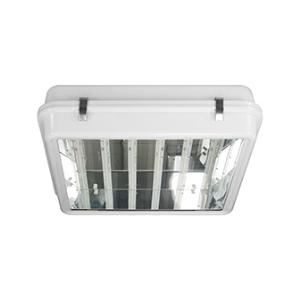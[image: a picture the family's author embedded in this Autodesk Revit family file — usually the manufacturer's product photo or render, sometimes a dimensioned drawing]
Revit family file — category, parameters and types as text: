
# Revit family: 3f_filippi_-_3f_cub_vt_3f_filippi_-_56332_-_3f_cub_led_100w_dali_cr_vt
name_source: partatom
category: Lighting Fixtures
units: mm (PartAtom-declared; Revit-internal decimal feet)

## family parameters
Cut with Voids When Loaded = No
Host = Face
Light Source = No
Part Type = Normal
Room Calculation Point = No
Round Connector Dimension = Use Diameter
Shared = No

## types (1)
- 3F Filippi - 3F Cub VT (1 x LED, 15195 lm, 108 W, 4000 K)
    Apparent Load = 108 VA
    Approval mark = CE
    CIE Flux Codes = 54 85 98 100 100
    Color Rendering = 80
    Color Temperature = 4000 K
    Control Gear = Electronic transformer
    Default Elevation = 1800 mm
    Description = ILLUMINOTECHNICAL
Luminous efficiency 100% (DLOR 100%, ULOR 0%).
Initial luminous flux of the luminaire 15195 lm.
Symmetric wide direct distribution.
Installation Interdistance Transv.D = 0.91 x hu - Long.D = 1.24 x hu.
Tabular UGR (CIE 117 - 4H-8H; S=0.25H; 70/50/20): RUG 23 - 25.
Beam angle: 81° - 108°.
Luminous efficacy 141 lm/W.
Lifetime (L90/B10): 30000 h. (tq+25°C)
Lifetime (L85/B10): 50000 h. (tq+25°C)
Lifetime (L80/B20): 80000 h. (tq+25°C)
Lifetime (L70/B20): 100000 h. (tq+25°C)
Lifetime (L70/B10): 50000 h. (tq+45°C)
Sudden decreased luminous flux after 50000 hours: 0% (C0).
Photobiological safety in compliance with IEC/TR 62778: RG0 risk exempt, (IEC 62471).
In compliance with IEC/EN 62722-2-1 - IEC/EN 62717 standards.

SOURCE
4 linear LED modules 25W/840.
Energy efficiency class (UE 2019/2020 - UE 2019/2015): C.
CIE 13.3 Colour rendering index: CRI >80 (R9 <50%).
IES TM-30 Fidelity Index: Rf = 84 Rg = 95.
CCT nominal colour temperature 4000 K.
Colour initial tolerance (MacAdam): SDCM 3.

MECHANICAL
Housing with double casing in pressed aluminium, powder-coated in white epoxy-polyester, hinged opening.
Quick connection in polycarbonate M20x1.5 cable gland for access to the terminal block.
Ecologic anti-aging injected sealing gasket.
Stainless steel clips.
Total flow recuperator in specular aluminium, with superficial titanium-magnesium treatment, non-iridescent.
Transparent, non-combustible tempered glass.
Fixing bracket for busbar or suspension in galvanised steel.
Luminaire with limited surface temperature. - D - (EN 60598-2-24)
Dimensions: 680x680 mm, height 187 mm. Weight 10.2 kg.
IP64 protection degree.
Mechanical strength to impacts IK10 (20 joule).
Glow-wire test resistance 960°C.

ELECTRICAL
Halogen Free DALI-2 DATI (Parts 251, 252, 253), PUSH-DIM, electronic wiring 230V-50/60Hz, power factor 0.95 at full load, THD <25%, constant output current, class I, 1 driver, 1 DALI addresse.
Power of the luminaire 108 W.
ENEC - CE.
SAFE FLICKER: PstLM=<1 and SVM=<0.4 (IEC TR 61547-1 and IEC TR 63158), to ensure a more comfortable and safe light.
Luminaire compliant with EN 60598-2-22 for power supply from a centralised emergency system CPSS (Central Power Supply System), not incorporated in the luminaire - high risk areas excluded. The default power and flux are 100% in AC and 15% in DC.
Ambient temperature from -20°C to +45°C.
Temperature class T6 max 85°C.
Quick connection.
Relative humidity UR: <85%.

INSTALLATION
Ceiling / Suspended.
All accessories dedicated to this product are available on the Catalog and on our website www.3F-Filippi.com.

APPLICATIONS
Areas with high ceilings, industrial/warehouses and open areas.

LIGHT MANAGEMENT
Recommended minimum setting: 10%.
The luminaire, equipped with (DALI-2 DATI) driver, can be controlled manually with 3F Easy Dim technology or automatically/manually with wired or wireless DALI/D2D control systems.
The D2D driver guarantees interoperability with other devices with the same certification by making the following information available:
Device Data (Part 251), Energy Report (Part 252), Diagnosis & Maintenance (Part 253).
In electrical systems without a regulation system (manual or automatic) and DALI bus, a suitable jumper must be made on the DA-DA terminals of the appliance.

WARNING
Fixture not suitable for cold stores with an ambient temperature <0°C and/or relative humidity >85%.
Luminaire designed for disposal/recycling at end-of-life.
Replaceable (LED only) light source by a professional. Replaceable control gear by a professional.
    Height = 187 mm
    Lamp = 1 x LED
    Lamp Light Flux = 15195 lm
    Lamp Power = 108 W
    Lamp count = 1
    Length = 680 mm
    Lifetime = 50000 h
    Luminous efficacy = 141 lm/W
    Manufacturer = 3F Filippi
    ModVariant = No
    Model = 3F Filippi - 56332 - 3F CUB LED 100W DALI CR VT
    Mounting Place = Ceiling
    Mounting Type = Pendant
    Number of Poles = 1
    OnlyDefault = Yes
    Power Factor = 1
    Product Name = 3F Filippi - 3F Cub VT
    Product group = pendant luminaire
    ProductGroupID = 9
    Protection Class = Protection class I
    Protection Degree = IP 64
    RLX_Detail_Level = 1
    RLX_Emergency_Light_Flux = 0 lm
    RLX_Emergency_Type = 0
    RLX_Emergency_Type_DB = No
    RlxData = <blob elided: 52353 chars, md5=3d49bf96>
    Socket = socket
    Standby Power = 0 W
    System Light Flux = 15195 lm
    System Power = 108 W
    Type Comments = Product without accessories
    Type Image = 3ffilippi_56332.jpg
    URL = http://relux.com
    VarID = ---
    Voltage = 0 V
    Weight = 0.00 kg
    Width = 680 mm

## geometry (parser evidence)
native form markers: Blend x4, Sweep x11
no freeform markers — native parametric forms only
